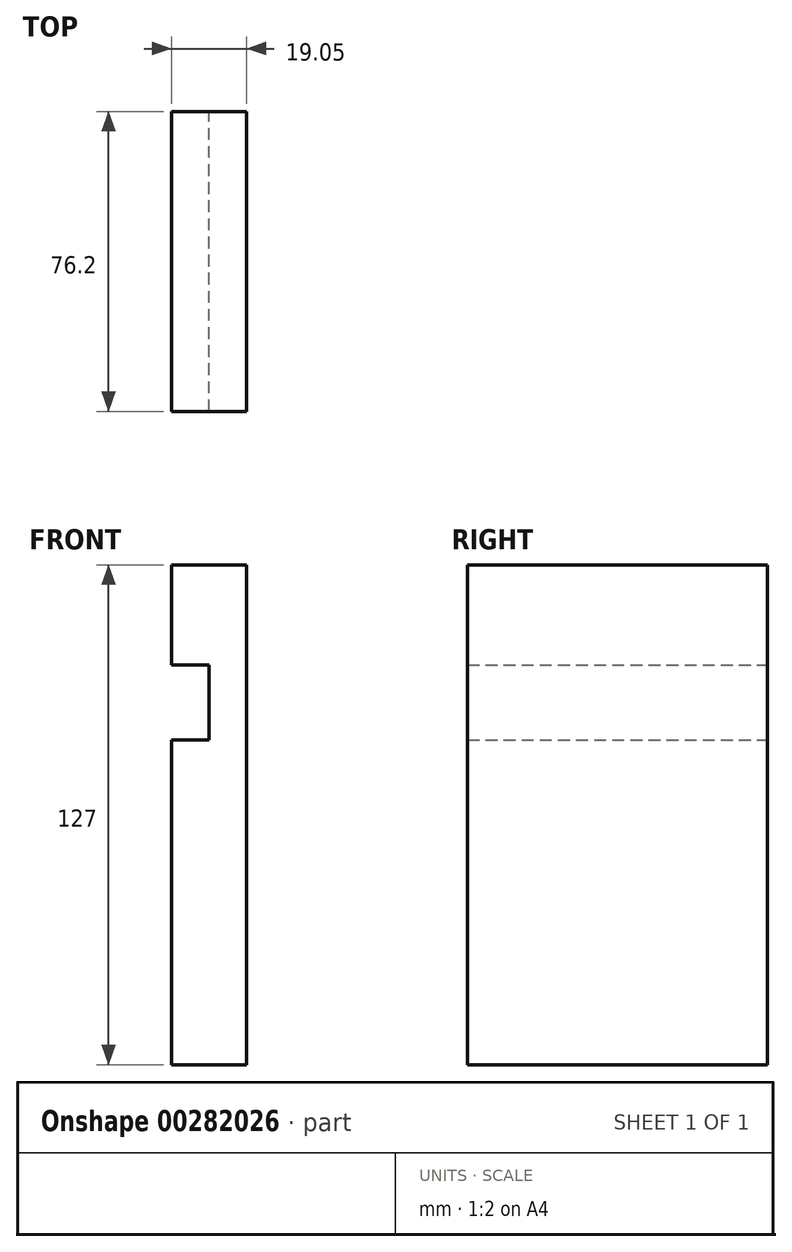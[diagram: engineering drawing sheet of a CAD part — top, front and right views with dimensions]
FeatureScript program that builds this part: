
annotation { "Feature Type Name" : "Feature", "Feature Type Description" : "" }
export const myFeature = defineFeature(function(context is Context, id is Id, definition is map)
    precondition{}
    {
        {
            var Q0;
            Q0=qCreatedBy(makeId("Front.planeOp"),FACE);
            var sketch = newSketch(context, id + "F0", { "sketchPlane" : qUnion([Q0])});
            skLineSegment(sketch, "E0", {"start": v(0, 0) * mm, "end": v(-19.05, 0) * mm});
            skLineSegment(sketch, "E1", {"start": v(-19.05, 0) * mm, "end": v(-19.05, 82.55) * mm});
            skLineSegment(sketch, "E2", {"start": v(-19.05, 82.55) * mm, "end": v(-9.53, 82.55) * mm});
            skLineSegment(sketch, "E3", {"start": v(-9.53, 82.55) * mm, "end": v(-9.53, 101.6) * mm});
            skLineSegment(sketch, "E4", {"start": v(-9.53, 101.6) * mm, "end": v(-19.05, 101.6) * mm});
            skLineSegment(sketch, "E5", {"start": v(-19.05, 101.6) * mm, "end": v(-19.05, 127) * mm});
            skLineSegment(sketch, "E6", {"start": v(-19.05, 127) * mm, "end": v(0, 127) * mm});
            skLineSegment(sketch, "E7", {"start": v(0, 127) * mm, "end": v(0, 0) * mm});
            skSolve(sketch);
        }
        {
            var Q0;
            Q0 = qSketchRegion(id + "F0", true);
            extrude(context, id + "F1", {"entities" : qUnion([Q0]), "depth" : 76.2 * mm});
        }
    });
